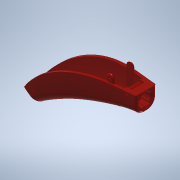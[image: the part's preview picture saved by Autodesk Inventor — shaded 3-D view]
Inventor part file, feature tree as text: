
AUTODESK INVENTOR PART (.ipt)
format: ipt  version: 2020 (Build 240168000, 168)  size: 8,567,808 bytes
history: native  units: in
note: dims shown in document units (in); Inventor stores cm internally (conversion verified against a paired STEP export)
features: fillet x16, sketch x15, extrude x14, delete_face x5, other x3, projected_geometry x3, chamfer x2, sweep x1, draft x1, mirror x1, boolean_combine x1, split x1
ambient origin geometry x8: Origin, YZ Plane, XZ Plane, XY Plane, X Axis, Y Axis, Z Axis, Center Point
bodies: Solid5 (feature_tree), Solid6 (feature_tree)
feature tree (63):
  other  "Part1b1.ipt"
  extrude  "Extrusion1"  Depth=1.1in
  sketch  "Sketch3-<F>"  dims[d18=0.625in d19=2.695in d20=0.268in d21=0.12in d22=0.3in d23=-0.0687in]
  sketch  "Sketch6-<F>"  dims[d25=0.78in d26=1.035in d30=0.18in]
  sketch  "3D Sketch2"
  sweep  "Sweep3"
  delete_face  "Delete Face22"
  delete_face  "Delete Face23"
  draft  "FaceDraft1"
  mirror  "Mirror2"
  fillet  "Fillet12"  Radius=0.975in
  fillet  "Fillet13"  Radius=0.26in
  delete_face  "Delete Face24"
  delete_face  "Delete Face25"
  fillet  "Fillet14"  Radius=0.405in
  fillet  "Fillet15"  Radius=0.725in
  extrude  "Extrusion2"  Depth=2.695in
  fillet  "Fillet16"  Radius=0.268in
  fillet  "Fillet17"  Radius=0.12in
  fillet  "Fillet18"  Radius=0.3in
  boolean_combine  "Combine3"
  extrude  "Extrusion5"  Depth=1.035in
  fillet  "Fillet19"  Radius=0.18in
  sketch  "Sketch8-<F>"  dims[d31=0.475in d32=0.7in]
  extrude  "Extrusion3"  Depth=0.7in
  extrude  "Extrusion4"  Depth=1.15in
  chamfer  "Chamfer1"  Distance=0.0412in
  sketch  "Sketch11-<F>"  dims[d33=0.975in d34=1.15in]
  extrude  "Extrusion6"  Depth=0.3937in
  fillet  "Fillet21"  Radius=0.75in
  extrude  "Extrusion7"  Depth=0.3937in
  fillet  "Fillet22"  Radius=0.425in
  sketch  "Sketch18"  dims[d7=0.78in d8=1.1in]
  split  "Split2"
  chamfer  "Chamfer4"  [1 undecoded]
  fillet  "Fillet28"  Radius=0.4947in
  extrude  "Extrusion17"  Depth=0.3937in
  fillet  "Fillet29"  Radius=0.03in
  extrude  "Extrusion11"  Depth=0.3937in
  fillet  "Fillet23"  Radius=0.0687in
  sketch  "Sketch15-<F>"  dims[d35=1.3in]
  extrude  "Extrusion12"  Depth=0.3937in
  fillet  "Fillet24"  Radius=0.475in
  extrude  "Extrusion13"  Depth=0.3937in
  delete_face  "Delete Face27"
  extrude  "Extrusion14"  Depth=0.3937in
  fillet  "Fillet26"  Radius=0.3937in
  fillet  "Fillet27"  Radius=0.08in
  extrude  "Extrusion15"  Depth=0.3937in
  extrude  "Extrusion16"  Depth=0.3937in
  sketch  "Sketch2-<F>"  dims[d36=0.1in]
  sketch  "Sketch7-<F>"  dims[d37=0.112in]
  other  "Solid1::Part1b1.ipt"
  other  "TaggingFeature1"
  sketch  "Sketch9-<F>"  dims[d38=0.14in]
  sketch  "Sketch10-<F>"  dims[d39=0.15in]
  sketch  "Sketch14-<F>"  dims[d40=0.145in]
  sketch  "Sketch16-<F>"  dims[d41=0.125in]
  projected_geometry  "Projected Loop1"
  projected_geometry  "Projected Loop2"
  sketch  "Sketch17-<F>"  dims[d42=0.09in d53=0.0412in d54=0.35in d55=0.75in d56=0.075in d57=0.425in d58=0.0in d59=0.0in d60=0.4947in d61=0.375in d62=0.03in d63=0.065in d107=0.0687in d108=0.225in d109=0.5in d110=0.625in d111=0.3937in d112=0.64in d113=0.0in d114=0.45in d115=0.1969in d116=0.7in d117=0.1969in d118=0.475in d119=0.3in d120=0.55in d121=0.1722in d122=0.08in d123=0.06in d124=0.125in d125=0.3937in d126=0.08in d127=0.06in d128=0.125in d129=0.3937in d130=0.045in d131=0.09in d132=0.115in d133=0.2461in d134=0.045in d135=0.09in d136=0.115in d137=0.2541in d139=0.052in d140=0.06in d141=0.198in d142=0.2554in d143=0.0in d144=0.008in d145=0.02in d146=0.03in d147=0.143in d148=0.1755in d149=0.023in d150=0.1in d151=0.008in d152=0.127in d153=0.108in d154=0.03in d155=0.3937in d156=0.101in d157=1.0in d158=0.0in d159=0.136in d160=0.0in d161=0.018in d162=0.016in d163=45.0deg d167=1.1501in d168=0.268in d169=1.512in d170=0.5in d171=0.7in d172=0.03in d173=0.03in d174=0.03in d175=0.166in d176=0.0in d177=0.01in d178=0.198in d179=0.2745in d180=0.5in d184=0.2752in d185=0.0in d187=0.0276in d188=0.0in d198=0.008in d199=0.008in d209=0.009in d210=0.009in d225=0.05in d226=0.125in d227=0.1374in d230=0.0362in d233=0.05in d234=0.012in d235=0.0625in d236=0.0635in d239=0.101in d240=0.0in d241=0.006in d243=0.07in d244=0.16in d245=0.317in d246=0.237in d247=0.022in d248=0.233in d249=0.0in d250=0.016in d251=0.189in d252=0.0in d253=0.05in d254=0.0in d256=0.002in d257=0.002in d258=0.275in d259=1.115in d260=0.022in d261=0.1577in d262=0.0in d263=0.15in d264=0.03in d265=0.0in d266=0.7578in d267=0.1in d268=0.0374in d272=0.1535in d273=0.189in d274=0.248in d275=0.0787in d276=0.0118in d277=0.0in d278=0.0154in d279=0.126in d280=0.0in d281=0.0039in d282=0.3436in d283=0.7559in d284=0.0079in d285=0.0004in d286=0.0079in d287=0.0079in]
  sketch  "Sketch19"  dims[d10=1.0in d13=2.75in d14=0.975in d15=0.26in d16=0.405in d17=0.725in]
  projected_geometry  "Projected Loop4"
note: 1 required parameter value undecoded (feature->parameter linkage not recoverable at this tier; creation-order binding heuristic only, values carry confidence <= 0.55)
